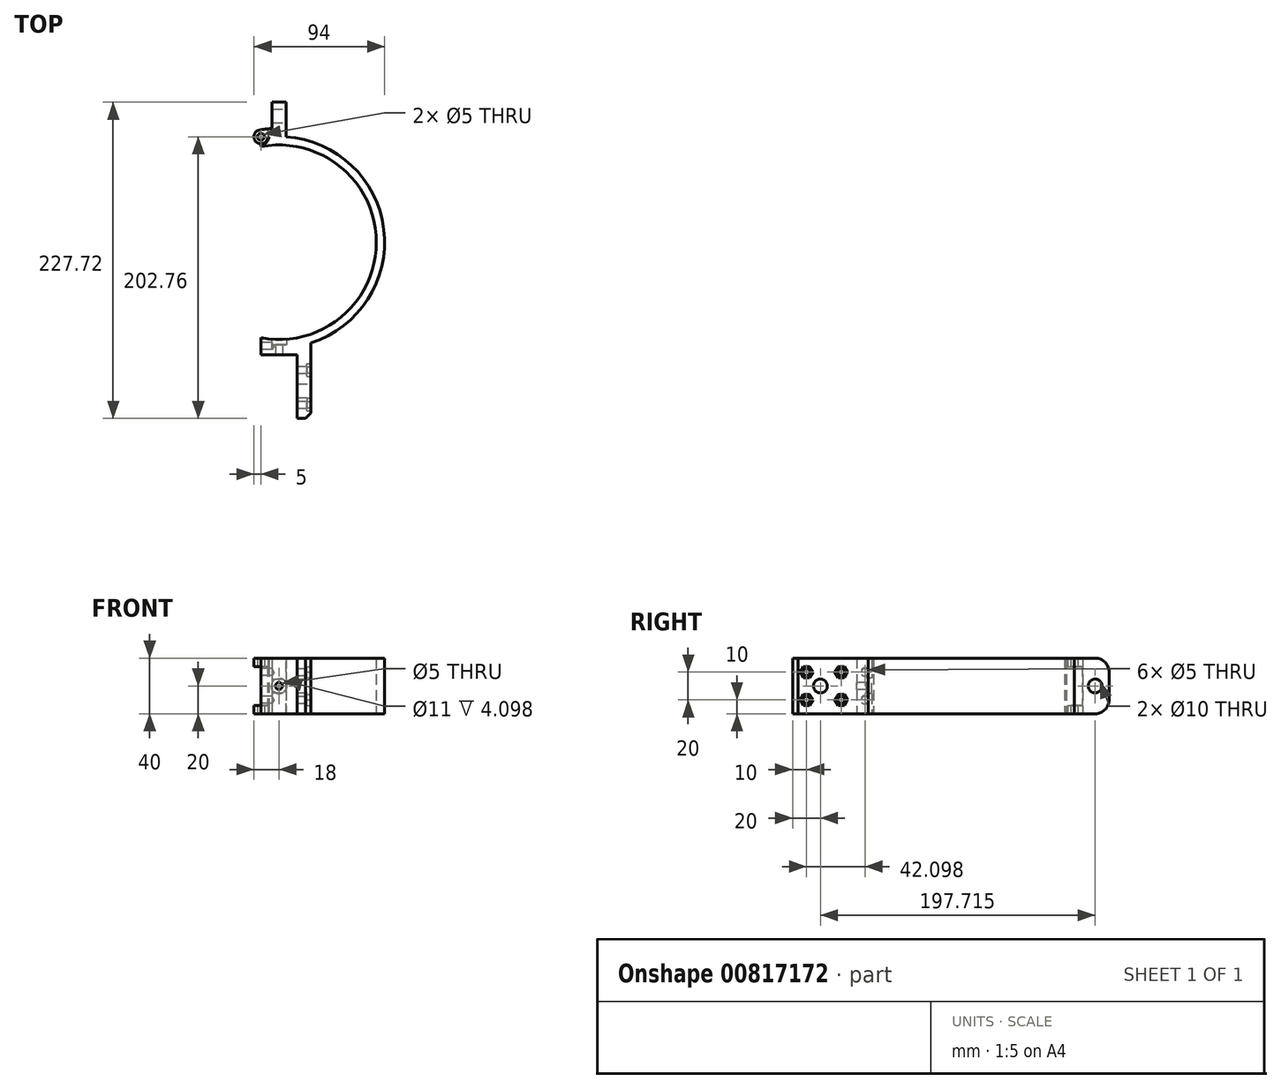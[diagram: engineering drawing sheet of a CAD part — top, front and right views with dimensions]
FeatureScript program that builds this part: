
annotation { "Feature Type Name" : "Feature", "Feature Type Description" : "" }
export const myFeature = defineFeature(function(context is Context, id is Id, definition is map)
    precondition{}
    {
        {
            var Q0;
            Q0=qCreatedBy(makeId("Top.planeOp"),FACE);
            var sketch = newSketch(context, id + "F0", { "sketchPlane" : qUnion([Q0])});
            skCircle(sketch, "E0", {"center": v(0, 0) * mm, "radius": 70 * mm});
            skCircle(sketch, "E1", {"center": v(0, 0) * mm, "radius": 76 * mm});
            skLineSegment(sketch, "E2", {"start": v(13, -74.88) * mm, "end": v(13, -126.88) * mm});
            skLineSegment(sketch, "E3", {"start": v(13, -126.88) * mm, "end": v(23, -126.88) * mm});
            skLineSegment(sketch, "E4", {"start": v(23, -126.88) * mm, "end": v(23, -72.44) * mm});
            skLineSegment(sketch, "E5", {"start": v(13, -80.88) * mm, "end": v(-13, -80.88) * mm});
            skLineSegment(sketch, "E6", {"start": v(-13, -80.88) * mm, "end": v(-13, -68.78) * mm});
            skLineSegment(sketch, "E7", {"start": v(-13, 68.78) * mm, "end": v(-13, 74.88) * mm});
            skPoint(sketch, "E8", {"position": v(-13, 75.88) * mm});
            skCircle(sketch, "E9", {"center": v(-13, 75.88) * mm, "radius": 5 * mm});
            skLineSegment(sketch, "E10", {"start": v(-5, 75.84) * mm, "end": v(-5, 100.84) * mm});
            skLineSegment(sketch, "E11", {"start": v(-5, 100.84) * mm, "end": v(5, 100.84) * mm});
            skLineSegment(sketch, "E12", {"start": v(5, 100.84) * mm, "end": v(5, 75.84) * mm});
            skArc(sketch, "E13", {"start": v(-13.9, 80.8) * mm, "mid": v(-9.46, 81.44) * mm, "end": v(-5, 81.83) * mm});
            skLineSegment(sketch, "E14", {"start": v(-7.31, 75.65) * mm, "end": v(-8.3, 81.56) * mm});
            skArc(sketch, "E15", {"start": v(-7.31, 75.65) * mm, "mid": v(-9.06, 71.77) * mm, "end": v(-13, 70.19) * mm});
            skSolve(sketch);
        }
        {
            var Q0;
            {var subQ3=sQuery(id+"F0.wireOp",EDGE,"E14");Q0=makeQuery(id+"F0.imprint","IMPRINT",FACE,{"disambiguationData":[TD([[makeQuery(id+"F0.imprint","IMPRINT",EDGE,{"derivedFrom":subQ3}),-1.0]])]});}
            var Q1;
            {var subQ0=sQuery(id+"F0.wireOp",EDGE,"E11");Q1=makeQuery(id+"F0.imprint","IMPRINT",FACE,{"disambiguationData":[TD([[makeQuery(id+"F0.imprint","IMPRINT",EDGE,{"derivedFrom":subQ0}),-1.0]])]});}
            var Q2;
            {var subQ6=sQuery(id+"F0.wireOp",EDGE,"E6");var subQ7=sQuery(id+"F0.wireOp",EDGE,"E0");var subQ8=makeQuery(id+"F0.imprint","INTERSECT",VERTEX,{"derivedFrom":[subQ7,subQ6]});Q2=makeQuery(id+"F0.imprint","IMPRINT",FACE,{"disambiguationData":[TD([[makeQuery(id+"F0.imprint","IMPRINT",EDGE,{"disambiguationData":[TD([[subQ8,-1.0]])],"derivedFrom":subQ7}),-1.0]])]});}
            var Q3;
            {var subQ5=sQuery(id+"F0.wireOp",EDGE,"E5");Q3=makeQuery(id+"F0.imprint","IMPRINT",FACE,{"disambiguationData":[TD([[makeQuery(id+"F0.imprint","IMPRINT",EDGE,{"derivedFrom":subQ5}),-1.0]])]});}
            var Q4;
            {var subQ0=sQuery(id+"F0.wireOp",EDGE,"E3");Q4=makeQuery(id+"F0.imprint","IMPRINT",FACE,{"disambiguationData":[TD([[makeQuery(id+"F0.imprint","IMPRINT",EDGE,{"derivedFrom":subQ0}),1.0]])]});}
            extrude(context, id + "F1", {"entities" : qUnion([Q0, Q1, Q2, Q3, Q4]), "depth" : 40 * mm, "offsetDistance" : 25 * mm});
        }
        {
            var Q0;
            {var subQ0=sQuery(id+"F0.wireOp",EDGE,"E14");Q0=makeQuery(id+"F0.imprint","IMPRINT",FACE,{"disambiguationData":[TD([[makeQuery(id+"F0.imprint","IMPRINT",EDGE,{"derivedFrom":subQ0}),1.0]])]});}
            var Q1;
            {var subQ0=sQuery(id+"F0.wireOp",EDGE,"E7");var subQ1=sQuery(id+"F0.wireOp",EDGE,"E1");var subQ2=makeQuery(id+"F0.imprint","INTERSECT",VERTEX,{"derivedFrom":[subQ1,subQ0]});Q1=makeQuery(id+"F0.imprint","IMPRINT",FACE,{"disambiguationData":[TD([[makeQuery(id+"F0.imprint","IMPRINT",EDGE,{"disambiguationData":[TD([[subQ2,1.0]])],"derivedFrom":subQ1}),1.0]])]});}
            var Q2;
            {var subQ0=sQuery(id+"F0.wireOp",EDGE,"E7");var subQ1=sQuery(id+"F0.wireOp",EDGE,"E1");var subQ2=makeQuery(id+"F0.imprint","INTERSECT",VERTEX,{"derivedFrom":[subQ1,subQ0]});Q2=makeQuery(id+"F0.imprint","IMPRINT",FACE,{"disambiguationData":[TD([[makeQuery(id+"F0.imprint","IMPRINT",EDGE,{"disambiguationData":[TD([[subQ2,-1.0]])],"derivedFrom":subQ1}),1.0]])]});}
            var Q3;
            {var subQ0=sQuery(id+"F0.wireOp",EDGE,"E1");var subQ1=makeQuery(id+"F0.imprint","INTERSECT",VERTEX,{"derivedFrom":[subQ0,sQuery(id+"F0.wireOp",EDGE,"E7")]});Q3=makeQuery(id+"F0.imprint","IMPRINT",FACE,{"disambiguationData":[TD([[makeQuery(id+"F0.imprint","IMPRINT",EDGE,{"disambiguationData":[TD([[subQ1,1.0]])],"derivedFrom":subQ0}),-1.0]])]});}
            var Q4;
            {var subQ0=sQuery(id+"F0.wireOp",EDGE,"E15");Q4=makeQuery(id+"F0.imprint","IMPRINT",FACE,{"disambiguationData":[TD([[makeQuery(id+"F0.imprint","IMPRINT",EDGE,{"derivedFrom":subQ0}),-1.0]])]});}
            extrude(context, id + "F2", {"entities" : qUnion([Q0, Q1, Q2, Q3, Q4]), "operationType" : NewBodyOperationType.ADD, "depth" : 40 * mm, "offsetDistance" : 25 * mm, "hasSecondDirection" : true, "secondDirectionOppositeDirection" : false, "secondDirectionDepth" : 34 * mm});
        }
        {
            var Q0;
            {var subQ0=sQuery(id+"F0.wireOp",EDGE,"E14");Q0=makeQuery(id+"F0.imprint","IMPRINT",FACE,{"disambiguationData":[TD([[makeQuery(id+"F0.imprint","IMPRINT",EDGE,{"derivedFrom":subQ0}),1.0]])]});}
            var Q1;
            {var subQ0=sQuery(id+"F0.wireOp",EDGE,"E7");var subQ1=sQuery(id+"F0.wireOp",EDGE,"E1");var subQ2=makeQuery(id+"F0.imprint","INTERSECT",VERTEX,{"derivedFrom":[subQ1,subQ0]});Q1=makeQuery(id+"F0.imprint","IMPRINT",FACE,{"disambiguationData":[TD([[makeQuery(id+"F0.imprint","IMPRINT",EDGE,{"disambiguationData":[TD([[subQ2,1.0]])],"derivedFrom":subQ1}),1.0]])]});}
            var Q2;
            {var subQ0=sQuery(id+"F0.wireOp",EDGE,"E7");var subQ1=sQuery(id+"F0.wireOp",EDGE,"E1");var subQ2=makeQuery(id+"F0.imprint","INTERSECT",VERTEX,{"derivedFrom":[subQ1,subQ0]});Q2=makeQuery(id+"F0.imprint","IMPRINT",FACE,{"disambiguationData":[TD([[makeQuery(id+"F0.imprint","IMPRINT",EDGE,{"disambiguationData":[TD([[subQ2,-1.0]])],"derivedFrom":subQ1}),1.0]])]});}
            var Q3;
            {var subQ0=sQuery(id+"F0.wireOp",EDGE,"E1");var subQ1=makeQuery(id+"F0.imprint","INTERSECT",VERTEX,{"derivedFrom":[subQ0,sQuery(id+"F0.wireOp",EDGE,"E7")]});Q3=makeQuery(id+"F0.imprint","IMPRINT",FACE,{"disambiguationData":[TD([[makeQuery(id+"F0.imprint","IMPRINT",EDGE,{"disambiguationData":[TD([[subQ1,1.0]])],"derivedFrom":subQ0}),-1.0]])]});}
            var Q4;
            {var subQ0=sQuery(id+"F0.wireOp",EDGE,"E15");Q4=makeQuery(id+"F0.imprint","IMPRINT",FACE,{"disambiguationData":[TD([[makeQuery(id+"F0.imprint","IMPRINT",EDGE,{"derivedFrom":subQ0}),-1.0]])]});}
            extrude(context, id + "F3", {"entities" : qUnion([Q0, Q1, Q2, Q3, Q4]), "operationType" : NewBodyOperationType.ADD, "depth" : 6 * mm, "offsetDistance" : 25 * mm});
        }
        {
            var Q0;
            Q0=makeQuery(id+"F1.opExtrude","SWEPT_FACE",FACE,{"disambiguationData":[OSD([sQuery(id+"F0.wireOp",EDGE,"E6")])]});
            var sketch = newSketch(context, id + "F4", { "sketchPlane" : qUnion([Q0])});
            skPoint(sketch, "E16", {"position": v(74.78, 30) * mm});
            skPoint(sketch, "E17", {"position": v(74.78, 10) * mm});
            skSolve(sketch);
        }
        {
            var Q0;
            Q0=sQuery(id+"F4.wireOp",VERTEX,"E16");
            var Q1;
            Q1=sQuery(id+"F4.wireOp",VERTEX,"E17");
            var Q2;
            Q2=makeQuery(id+"F1.opExtrude","SWEPT_BODY",BODY,{"disambiguationData":[OSD([sQuery(id+"F0.wireOp",EDGE,"E0"),sQuery(id+"F0.wireOp",EDGE,"E1"),sQuery(id+"F0.wireOp",EDGE,"E2"),sQuery(id+"F0.wireOp",EDGE,"E3"),sQuery(id+"F0.wireOp",EDGE,"E4"),sQuery(id+"F0.wireOp",EDGE,"E5"),sQuery(id+"F0.wireOp",EDGE,"E6"),sQuery(id+"F0.wireOp",EDGE,"E7"),sQuery(id+"F0.wireOp",EDGE,"E9"),sQuery(id+"F0.wireOp",EDGE,"E10"),sQuery(id+"F0.wireOp",EDGE,"E11"),sQuery(id+"F0.wireOp",EDGE,"E12"),sQuery(id+"F0.wireOp",EDGE,"E13"),sQuery(id+"F0.wireOp",EDGE,"E14")])]});
            hole(context, id + "F5", {"style" : HoleStyle.C_SINK, "endStyle" : HoleEndStyle.BLIND, "holeDiameter" : 5 * mm, "cSinkDiameter" : 6 * mm, "cSinkAngle" : 90 * degree, "majorDiameter" : 5 * mm, "holeDepth" : 8 * mm, "isTappedThrough" : true, "tappedDepth" : 12 * mm, "tapClearance" : 3, "locations" : qUnion([Q0, Q1]), "scope" : qUnion([Q2])});
        }
        {
            var Q0;
            Q0=makeQuery(id+"F1.opExtrude","SWEPT_FACE",FACE,{"disambiguationData":[OSD([sQuery(id+"F0.wireOp",EDGE,"E4")])]});
            var sketch = newSketch(context, id + "F6", { "sketchPlane" : qUnion([Q0])});
            skPoint(sketch, "E18", {"position": v(-106.88, 20) * mm});
            skPoint(sketch, "E19", {"position": v(-116.88, 30) * mm});
            skPoint(sketch, "E20", {"position": v(-91.88, 30) * mm});
            skPoint(sketch, "E21", {"position": v(-91.88, 10) * mm});
            skPoint(sketch, "E22", {"position": v(-116.88, 10) * mm});
            skLineSegment(sketch, "E23", {"start": v(-94.73, 34) * mm, "end": v(-89.53, 34) * mm});
            skLineSegment(sketch, "E24.1.0", {"start": v(-96.77, 29.53) * mm, "end": v(-94.17, 34.03) * mm});
            skLineSegment(sketch, "E24.2.0", {"start": v(-93.92, 25.53) * mm, "end": v(-96.52, 30.03) * mm});
            skLineSegment(sketch, "E24.3.0", {"start": v(-89.03, 26) * mm, "end": v(-94.23, 26) * mm});
            skLineSegment(sketch, "E24.4.0", {"start": v(-86.99, 30.47) * mm, "end": v(-89.59, 25.97) * mm});
            skLineSegment(sketch, "E24.5.0", {"start": v(-89.84, 34.47) * mm, "end": v(-87.24, 29.97) * mm});
            skLineSegment(sketch, "E25.1.0.0", {"start": v(-119.73, 34) * mm, "end": v(-114.53, 34) * mm});
            skLineSegment(sketch, "E25.1.0.1", {"start": v(-114.84, 34.47) * mm, "end": v(-112.24, 29.97) * mm});
            skLineSegment(sketch, "E25.1.0.2", {"start": v(-111.99, 30.47) * mm, "end": v(-114.59, 25.97) * mm});
            skLineSegment(sketch, "E25.1.0.3", {"start": v(-114.03, 26) * mm, "end": v(-119.23, 26) * mm});
            skLineSegment(sketch, "E25.1.0.4", {"start": v(-118.92, 25.53) * mm, "end": v(-121.52, 30.03) * mm});
            skLineSegment(sketch, "E25.1.0.5", {"start": v(-121.77, 29.53) * mm, "end": v(-119.17, 34.03) * mm});
            skLineSegment(sketch, "E25.direction1", {"start": v(-94.73, 34) * mm, "end": v(-119.73, 34) * mm, "construction": true});
            skLineSegment(sketch, "E26.0.1.0", {"start": v(-121.77, 9.53) * mm, "end": v(-119.17, 14.03) * mm});
            skLineSegment(sketch, "E26.0.1.1", {"start": v(-114.03, 6) * mm, "end": v(-119.23, 6) * mm});
            skLineSegment(sketch, "E26.0.1.2", {"start": v(-114.84, 14.47) * mm, "end": v(-112.24, 9.97) * mm});
            skLineSegment(sketch, "E26.0.1.3", {"start": v(-94.73, 14) * mm, "end": v(-119.73, 14) * mm, "construction": true});
            skLineSegment(sketch, "E26.0.1.4", {"start": v(-118.92, 5.53) * mm, "end": v(-121.52, 10.03) * mm});
            skLineSegment(sketch, "E26.0.1.6", {"start": v(-89.84, 14.47) * mm, "end": v(-87.24, 9.97) * mm});
            skLineSegment(sketch, "E26.0.1.8", {"start": v(-93.92, 5.53) * mm, "end": v(-96.52, 10.03) * mm});
            skLineSegment(sketch, "E26.0.1.9", {"start": v(-94.73, 14) * mm, "end": v(-89.53, 14) * mm});
            skLineSegment(sketch, "E26.0.1.10", {"start": v(-89.03, 6) * mm, "end": v(-94.23, 6) * mm});
            skLineSegment(sketch, "E26.0.1.11", {"start": v(-86.99, 10.47) * mm, "end": v(-89.59, 5.97) * mm});
            skLineSegment(sketch, "E26.0.1.12", {"start": v(-96.77, 9.53) * mm, "end": v(-94.17, 14.03) * mm});
            skLineSegment(sketch, "E26.0.1.13", {"start": v(-119.73, 14) * mm, "end": v(-114.53, 14) * mm});
            skLineSegment(sketch, "E26.0.1.14", {"start": v(-111.99, 10.47) * mm, "end": v(-114.59, 5.97) * mm});
            skLineSegment(sketch, "E26.direction1", {"start": v(-119.23, 26) * mm, "end": v(-94.6, 26) * mm, "construction": true});
            skLineSegment(sketch, "E26.direction2", {"start": v(-119.23, 26) * mm, "end": v(-119.23, 6) * mm, "construction": true});
            skSolve(sketch);
        }
        {
            var Q0;
            Q0=sQuery(id+"F6.wireOp",VERTEX,"E18");
            var Q1;
            Q1=makeQuery(id+"F1.opExtrude","SWEPT_BODY",BODY,{"disambiguationData":[OSD([sQuery(id+"F0.wireOp",EDGE,"E0"),sQuery(id+"F0.wireOp",EDGE,"E1"),sQuery(id+"F0.wireOp",EDGE,"E2"),sQuery(id+"F0.wireOp",EDGE,"E3"),sQuery(id+"F0.wireOp",EDGE,"E4"),sQuery(id+"F0.wireOp",EDGE,"E5"),sQuery(id+"F0.wireOp",EDGE,"E6"),sQuery(id+"F0.wireOp",EDGE,"E7"),sQuery(id+"F0.wireOp",EDGE,"E9"),sQuery(id+"F0.wireOp",EDGE,"E10"),sQuery(id+"F0.wireOp",EDGE,"E11"),sQuery(id+"F0.wireOp",EDGE,"E12"),sQuery(id+"F0.wireOp",EDGE,"E13"),sQuery(id+"F0.wireOp",EDGE,"E14")])]});
            hole(context, id + "F7", {"style" : HoleStyle.SIMPLE, "endStyle" : HoleEndStyle.THROUGH, "holeDiameter" : 10 * mm, "majorDiameter" : 5 * mm, "isTappedThrough" : true, "tappedDepth" : 12 * mm, "tapClearance" : 3, "locations" : qUnion([Q0]), "scope" : qUnion([Q1])});
        }
        {
            var Q0;
            Q0=sQuery(id+"F6.wireOp",VERTEX,"E19");
            var Q1;
            Q1=sQuery(id+"F6.wireOp",VERTEX,"E20");
            var Q2;
            Q2=sQuery(id+"F6.wireOp",VERTEX,"E21");
            var Q3;
            Q3=sQuery(id+"F6.wireOp",VERTEX,"E22");
            var Q4;
            Q4=makeQuery(id+"F1.opExtrude","SWEPT_BODY",BODY,{"disambiguationData":[OSD([sQuery(id+"F0.wireOp",EDGE,"E0"),sQuery(id+"F0.wireOp",EDGE,"E1"),sQuery(id+"F0.wireOp",EDGE,"E2"),sQuery(id+"F0.wireOp",EDGE,"E3"),sQuery(id+"F0.wireOp",EDGE,"E4"),sQuery(id+"F0.wireOp",EDGE,"E5"),sQuery(id+"F0.wireOp",EDGE,"E6"),sQuery(id+"F0.wireOp",EDGE,"E7"),sQuery(id+"F0.wireOp",EDGE,"E9"),sQuery(id+"F0.wireOp",EDGE,"E10"),sQuery(id+"F0.wireOp",EDGE,"E11"),sQuery(id+"F0.wireOp",EDGE,"E12"),sQuery(id+"F0.wireOp",EDGE,"E13"),sQuery(id+"F0.wireOp",EDGE,"E14")])]});
            hole(context, id + "F8", {"style" : HoleStyle.SIMPLE, "endStyle" : HoleEndStyle.THROUGH, "holeDiameter" : 5 * mm, "majorDiameter" : 5 * mm, "isTappedThrough" : true, "tappedDepth" : 12 * mm, "tapClearance" : 3, "locations" : qUnion([Q0, Q1, Q2, Q3]), "scope" : qUnion([Q4])});
        }
        {
            var Q0;
            Q0=makeQuery(id+"F1.opExtrude","SWEPT_EDGE",EDGE,{"disambiguationData":[OSD([sQuery(id+"F0.wireOp",EDGE,"E3"),sQuery(id+"F0.wireOp",EDGE,"E4")])]});
            chamfer(context, id + "F9", {"entities" : qUnion([Q0]), "width" : 4 * mm, "tangentPropagation" : true});
        }
        {
            var Q0;
            Q0=makeQuery(id+"F1.opExtrude","SWEPT_FACE",FACE,{"disambiguationData":[OSD([sQuery(id+"F0.wireOp",EDGE,"E12")])]});
            var sketch = newSketch(context, id + "F10", { "sketchPlane" : qUnion([Q0])});
            skPoint(sketch, "E27", {"position": v(90.84, 20) * mm});
            skSolve(sketch);
        }
        {
            var Q0;
            Q0=sQuery(id+"F10.wireOp",VERTEX,"E27");
            var Q1;
            Q1=makeQuery(id+"F1.opExtrude","SWEPT_BODY",BODY,{"disambiguationData":[OSD([sQuery(id+"F0.wireOp",EDGE,"E0"),sQuery(id+"F0.wireOp",EDGE,"E1"),sQuery(id+"F0.wireOp",EDGE,"E2"),sQuery(id+"F0.wireOp",EDGE,"E3"),sQuery(id+"F0.wireOp",EDGE,"E4"),sQuery(id+"F0.wireOp",EDGE,"E5"),sQuery(id+"F0.wireOp",EDGE,"E6"),sQuery(id+"F0.wireOp",EDGE,"E7"),sQuery(id+"F0.wireOp",EDGE,"E9"),sQuery(id+"F0.wireOp",EDGE,"E10"),sQuery(id+"F0.wireOp",EDGE,"E11"),sQuery(id+"F0.wireOp",EDGE,"E12"),sQuery(id+"F0.wireOp",EDGE,"E13"),sQuery(id+"F0.wireOp",EDGE,"E14")])]});
            hole(context, id + "F11", {"style" : HoleStyle.SIMPLE, "endStyle" : HoleEndStyle.THROUGH, "holeDiameter" : 10 * mm, "majorDiameter" : 5 * mm, "isTappedThrough" : true, "tappedDepth" : 12 * mm, "tapClearance" : 3, "locations" : qUnion([Q0]), "scope" : qUnion([Q1])});
        }
        {
            var Q0;
            Q0=makeQuery(id+"F1.opExtrude","CAP_EDGE",EDGE,{"disambiguationData":[OSD([sQuery(id+"F0.wireOp",EDGE,"E11")])],"isStart":false});
            var Q1;
            Q1=makeQuery(id+"F1.opExtrude","CAP_EDGE",EDGE,{"disambiguationData":[OSD([sQuery(id+"F0.wireOp",EDGE,"E11")])],"isStart":true});
            fillet(context, id + "F12", {"entities" : qUnion([Q0, Q1]), "radius" : 10 * mm, "tangentPropagation" : true, "allowEdgeOverflow" : false});
        }
        {
            var Q0;
            Q0=sQuery(id+"F0.wireOp",VERTEX,"E8");
            var Q1;
            Q1=makeQuery(id+"F1.opExtrude","SWEPT_BODY",BODY,{"disambiguationData":[OSD([sQuery(id+"F0.wireOp",EDGE,"E0"),sQuery(id+"F0.wireOp",EDGE,"E1"),sQuery(id+"F0.wireOp",EDGE,"E2"),sQuery(id+"F0.wireOp",EDGE,"E3"),sQuery(id+"F0.wireOp",EDGE,"E4"),sQuery(id+"F0.wireOp",EDGE,"E5"),sQuery(id+"F0.wireOp",EDGE,"E6"),sQuery(id+"F0.wireOp",EDGE,"E7"),sQuery(id+"F0.wireOp",EDGE,"E9"),sQuery(id+"F0.wireOp",EDGE,"E10"),sQuery(id+"F0.wireOp",EDGE,"E11"),sQuery(id+"F0.wireOp",EDGE,"E12"),sQuery(id+"F0.wireOp",EDGE,"E13"),sQuery(id+"F0.wireOp",EDGE,"E14")])]});
            hole(context, id + "F13", {"style" : HoleStyle.SIMPLE, "endStyle" : HoleEndStyle.THROUGH, "oppositeDirection" : true, "holeDiameter" : 5 * mm, "majorDiameter" : 5 * mm, "isTappedThrough" : true, "tappedDepth" : 12 * mm, "tapClearance" : 3, "locations" : qUnion([Q0]), "scope" : qUnion([Q1])});
        }
        {
            var Q0;
            Q0=makeQuery(id+"F1.opExtrude","SWEPT_FACE",FACE,{"disambiguationData":[OSD([sQuery(id+"F0.wireOp",EDGE,"E5")])]});
            var sketch = newSketch(context, id + "F14", { "sketchPlane" : qUnion([Q0])});
            skPoint(sketch, "E28", {"position": v(0, 20) * mm});
            skCircle(sketch, "E29", {"center": v(0, 20) * mm, "radius": 5.5 * mm});
            skSolve(sketch);
        }
        {
            var Q0;
            Q0=sQuery(id+"F14.wireOp",VERTEX,"E28");
            var Q1;
            Q1=makeQuery(id+"F1.opExtrude","SWEPT_BODY",BODY,{"disambiguationData":[OSD([sQuery(id+"F0.wireOp",EDGE,"E0"),sQuery(id+"F0.wireOp",EDGE,"E1"),sQuery(id+"F0.wireOp",EDGE,"E2"),sQuery(id+"F0.wireOp",EDGE,"E3"),sQuery(id+"F0.wireOp",EDGE,"E4"),sQuery(id+"F0.wireOp",EDGE,"E5"),sQuery(id+"F0.wireOp",EDGE,"E6"),sQuery(id+"F0.wireOp",EDGE,"E7"),sQuery(id+"F0.wireOp",EDGE,"E9"),sQuery(id+"F0.wireOp",EDGE,"E10"),sQuery(id+"F0.wireOp",EDGE,"E11"),sQuery(id+"F0.wireOp",EDGE,"E12"),sQuery(id+"F0.wireOp",EDGE,"E13"),sQuery(id+"F0.wireOp",EDGE,"E14")])]});
            hole(context, id + "F15", {"style" : HoleStyle.SIMPLE, "endStyle" : HoleEndStyle.BLIND, "holeDiameter" : 5 * mm, "majorDiameter" : 5 * mm, "holeDepth" : 12 * mm, "isTappedThrough" : true, "tappedDepth" : 12 * mm, "tapClearance" : 3, "locations" : qUnion([Q0]), "scope" : qUnion([Q1])});
        }
        {
            var Q0;
            Q0 = qSketchRegion(id + "F14", true);
            extrude(context, id + "F16", {"entities" : qUnion([Q0]), "operationType" : NewBodyOperationType.REMOVE, "oppositeDirection" : true, "depth" : 12 * mm, "offsetDistance" : 25 * mm, "hasSecondDirection" : true, "secondDirectionOppositeDirection" : true, "secondDirectionDepth" : 7 * mm});
        }
        {
            var Q0;
            {var subQ5=sQuery(id+"F6.wireOp",EDGE,"E25.1.0.1");var subQ7=sQuery(id+"F6.wireOp",EDGE,"E25.1.0.0");var subQ8=makeQuery(id+"F6.imprint","INTERSECT",VERTEX,{"derivedFrom":[subQ7,subQ5]});Q0=makeQuery(id+"F6.imprint","IMPRINT",FACE,{"disambiguationData":[TD([[makeQuery(id+"F6.imprint","IMPRINT",EDGE,{"disambiguationData":[TD([[subQ8,1.0]])],"derivedFrom":subQ7}),-1.0]])]});}
            var Q1;
            {var subQ5=sQuery(id+"F6.wireOp",EDGE,"E24.1.0");var subQ7=sQuery(id+"F6.wireOp",EDGE,"E23");var subQ8=makeQuery(id+"F6.imprint","INTERSECT",VERTEX,{"derivedFrom":[subQ7,subQ5]});Q1=makeQuery(id+"F6.imprint","IMPRINT",FACE,{"disambiguationData":[TD([[makeQuery(id+"F6.imprint","IMPRINT",EDGE,{"disambiguationData":[TD([[subQ8,-1.0]])],"derivedFrom":subQ7}),-1.0]])]});}
            var Q2;
            {var subQ5=sQuery(id+"F6.wireOp",EDGE,"E26.0.1.9");var subQ6=sQuery(id+"F6.wireOp",EDGE,"E26.0.1.6");var subQ7=makeQuery(id+"F6.imprint","INTERSECT",VERTEX,{"derivedFrom":[subQ6,subQ5]});Q2=makeQuery(id+"F6.imprint","IMPRINT",FACE,{"disambiguationData":[TD([[makeQuery(id+"F6.imprint","IMPRINT",EDGE,{"disambiguationData":[TD([[subQ7,-1.0]])],"derivedFrom":subQ6}),-1.0]])]});}
            var Q3;
            {var subQ0=sQuery(id+"F6.wireOp",EDGE,"E26.0.1.4");var subQ1=sQuery(id+"F6.wireOp",EDGE,"E26.0.1.0");var subQ2=makeQuery(id+"F6.imprint","INTERSECT",VERTEX,{"derivedFrom":[subQ1,subQ0]});Q3=makeQuery(id+"F6.imprint","IMPRINT",FACE,{"disambiguationData":[TD([[makeQuery(id+"F6.imprint","IMPRINT",EDGE,{"disambiguationData":[TD([[subQ2,-1.0]])],"derivedFrom":subQ1}),-1.0]])]});}
            extrude(context, id + "F17", {"entities" : qUnion([Q0, Q1, Q2, Q3]), "operationType" : NewBodyOperationType.REMOVE, "oppositeDirection" : true, "depth" : 3 * mm, "offsetDistance" : 25 * mm});
        }
    });
